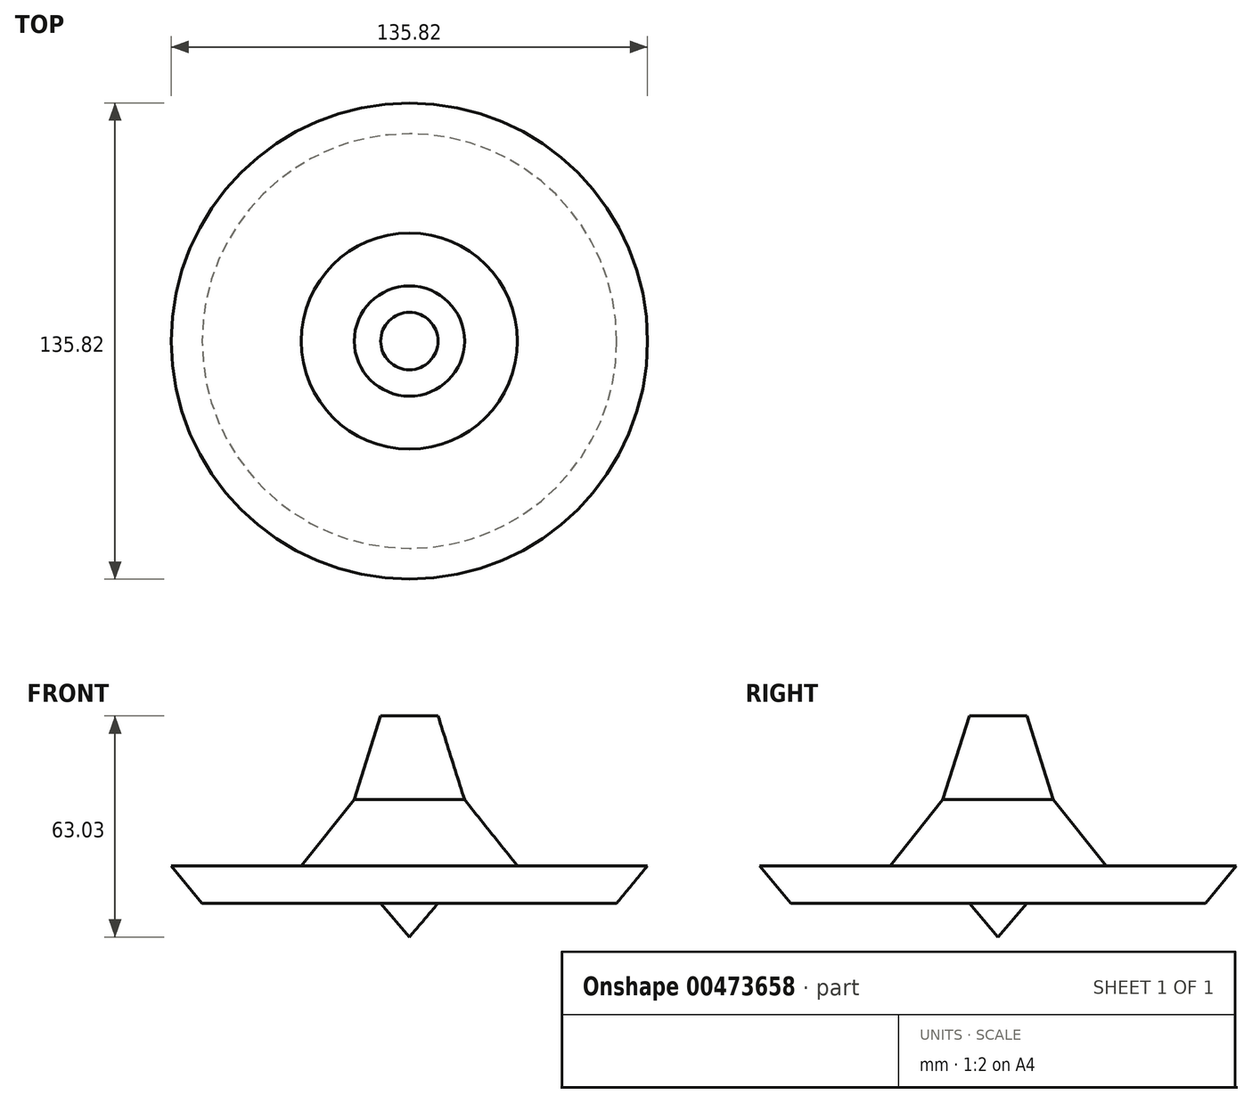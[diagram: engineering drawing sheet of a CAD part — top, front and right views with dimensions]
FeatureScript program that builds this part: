
annotation { "Feature Type Name" : "Feature", "Feature Type Description" : "" }
export const myFeature = defineFeature(function(context is Context, id is Id, definition is map)
    precondition{}
    {
        {
            var Q0;
            Q0=qCreatedBy(makeId("Front.planeOp"),FACE);
            var sketch = newSketch(context, id + "F0", { "sketchPlane" : qUnion([Q0])});
            skLineSegment(sketch, "E0", {"start": v(0, 0) * mm, "end": v(8.17, 9.59) * mm});
            skLineSegment(sketch, "E1", {"start": v(8.17, 9.59) * mm, "end": v(59.1, 9.59) * mm});
            skLineSegment(sketch, "E2", {"start": v(59.1, 9.59) * mm, "end": v(67.9, 20.28) * mm});
            skLineSegment(sketch, "E3", {"start": v(67.9, 20.28) * mm, "end": v(30.8, 20.28) * mm});
            skLineSegment(sketch, "E4", {"start": v(30.8, 20.28) * mm, "end": v(15.72, 39.14) * mm});
            skLineSegment(sketch, "E5", {"start": v(15.72, 39.14) * mm, "end": v(8.17, 63.03) * mm});
            skLineSegment(sketch, "E6", {"start": v(8.17, 63.03) * mm, "end": v(0, 63.03) * mm});
            skLineSegment(sketch, "E7", {"start": v(0, 63.03) * mm, "end": v(0, 0) * mm});
            skSolve(sketch);
        }
        {
            var Q0;
            Q0=makeQuery(id+"F0.imprint","IMPRINT",FACE,{"disambiguationData":[TD([[makeQuery(id+"F0.imprint","IMPRINT",EDGE,{"derivedFrom":sQuery(id+"F0.wireOp",EDGE,"E0")}),1.0]])]});
            var Q1;
            Q1=sQuery(id+"F0.wireOp",EDGE,"E7");
            revolve(context, id + "F1", {"entities" : qUnion([Q0]), "axis" : qUnion([Q1]), "revolveType" : RevolveType.FULL});
        }
    });
